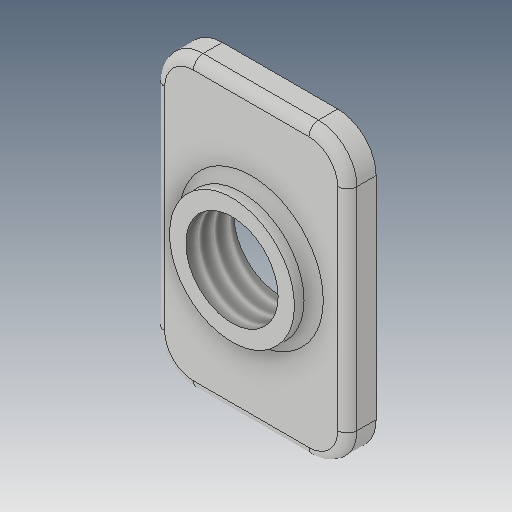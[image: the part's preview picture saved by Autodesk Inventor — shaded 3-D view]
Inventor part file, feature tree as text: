
AUTODESK INVENTOR PART (.ipt)
format: ipt  version: 2017 (Build 210142000, 142)  size: 176,128 bytes
history: native  units: mm
features: extrude x2, fillet x2, sketch x2, thread x1
ambient origin geometry x8: Origin, YZ Plane, XZ Plane, XY Plane, X Axis, Y Axis, Z Axis, Center Point
bodies: Solid1 (feature_tree)
feature tree (7):
  extrude  "Extrusion1"  Depth=15.0mm
  extrude  "Extrusion2"  Depth=2.0mm
  fillet  "Fillet1"  Radius=1.5mm
  thread  "Thread1"  [1 undecoded]
  fillet  "Fillet2"  Radius=1.0mm
  sketch  "Sketch1"  dims[d0=10.0mm d1=15.0mm]
  sketch  "Sketch2"  dims[d2=4.8mm d3=2.0mm d4=1.5mm d5=0.0mm d6=6.5mm d7=1.0mm d8=0.0mm d9=0.5mm d10=10.0mm d11=0.0mm d12=0.5mm]
note: 1 required parameter value undecoded (feature->parameter linkage not recoverable at this tier; creation-order binding heuristic only, values carry confidence <= 0.55)
